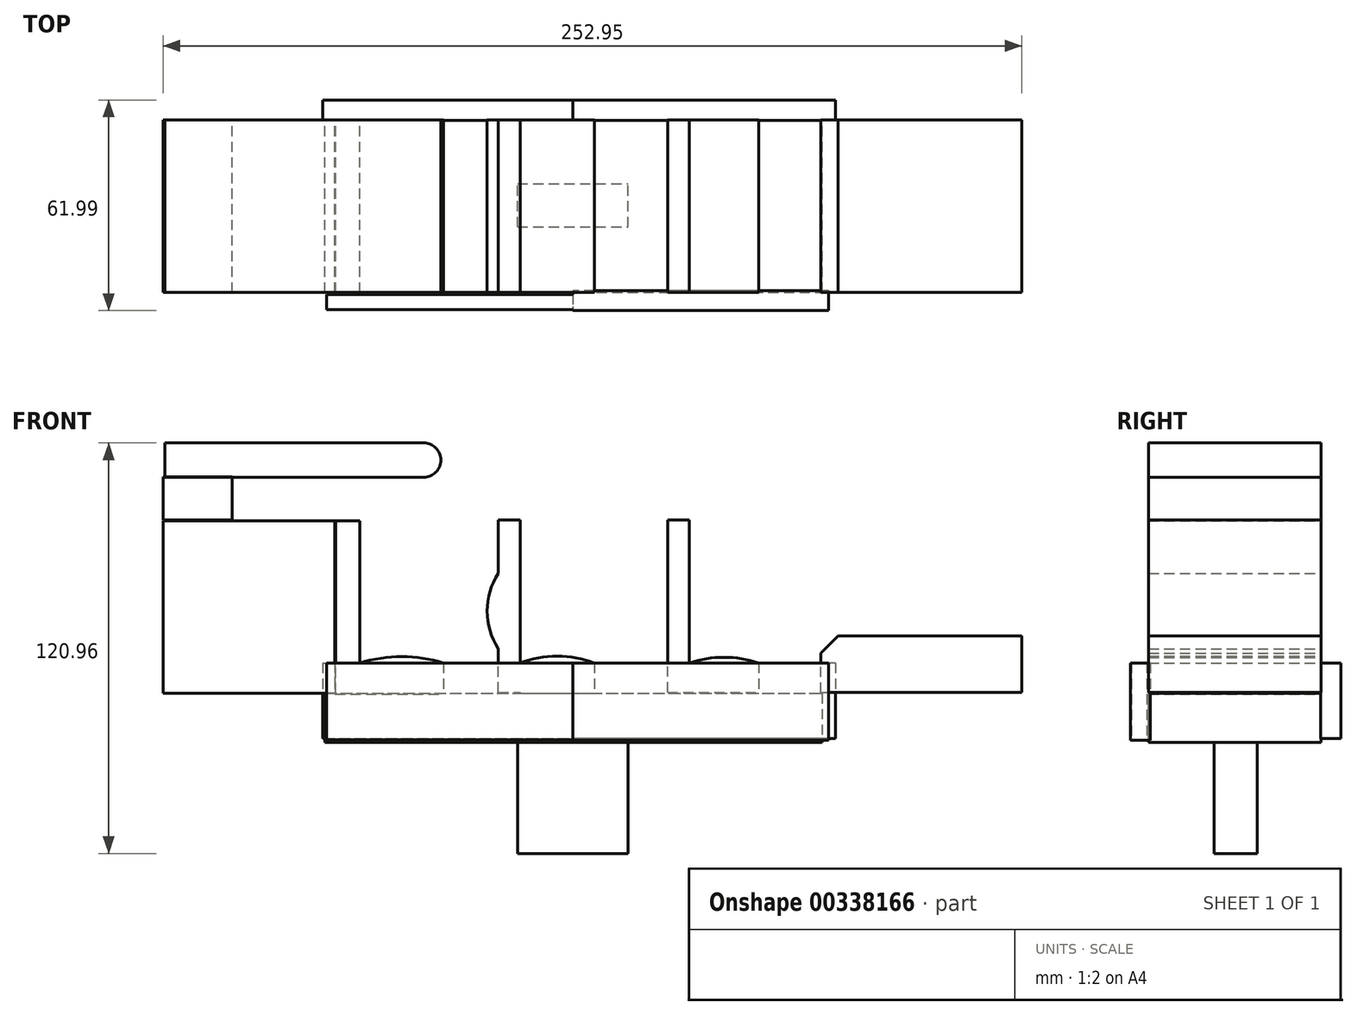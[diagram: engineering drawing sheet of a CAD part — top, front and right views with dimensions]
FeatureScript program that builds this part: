
annotation { "Feature Type Name" : "Feature", "Feature Type Description" : "" }
export const myFeature = defineFeature(function(context is Context, id is Id, definition is map)
    precondition{}
    {
        {
            var Q0;
            Q0=qCreatedBy(makeId("Front.planeOp"),FACE);
            var sketch = newSketch(context, id + "F0", { "sketchPlane" : qUnion([Q0])});
            skLineSegment(sketch, "E0.bottom", {"start": v(-72.96, -23.33) * mm, "end": v(-22.26, -23.33) * mm});
            skLineSegment(sketch, "E0.top", {"start": v(-72.96, -8.96) * mm, "end": v(-22.26, -8.96) * mm});
            skLineSegment(sketch, "E0.left", {"start": v(-72.96, -23.33) * mm, "end": v(-72.96, -8.96) * mm});
            skLineSegment(sketch, "E0.right", {"start": v(-22.26, -23.33) * mm, "end": v(-22.26, -8.96) * mm});
            skLineSegment(sketch, "E1.bottom", {"start": v(-22.26, -8.96) * mm, "end": v(28.07, -8.96) * mm});
            skLineSegment(sketch, "E1.top", {"start": v(-22.26, -23.33) * mm, "end": v(28.07, -23.33) * mm});
            skLineSegment(sketch, "E1.left", {"start": v(-22.26, -8.96) * mm, "end": v(-22.26, -23.33) * mm});
            skLineSegment(sketch, "E1.right", {"start": v(28.07, -8.96) * mm, "end": v(28.07, -23.33) * mm});
            skLineSegment(sketch, "E2.bottom", {"start": v(28.07, -8.96) * mm, "end": v(73.47, -8.96) * mm});
            skLineSegment(sketch, "E2.top", {"start": v(28.07, -23.33) * mm, "end": v(73.47, -23.33) * mm});
            skLineSegment(sketch, "E2.right", {"start": v(73.47, -8.96) * mm, "end": v(73.47, -23.33) * mm});
            skSolve(sketch);
        }
        {
            var Q0;
            Q0=qCreatedBy(makeId("Front.planeOp"),FACE);
            var sketch = newSketch(context, id + "F1", { "sketchPlane" : qUnion([Q0])});
            skLineSegment(sketch, "E3.bottom", {"start": v(-69.87, -8.9) * mm, "end": v(-120.67, -8.9) * mm});
            skLineSegment(sketch, "E3.top", {"start": v(-69.87, 41.9) * mm, "end": v(-120.67, 41.9) * mm});
            skLineSegment(sketch, "E3.left", {"start": v(-69.87, -8.9) * mm, "end": v(-69.87, 41.9) * mm});
            skLineSegment(sketch, "E3.right", {"start": v(-120.67, -8.9) * mm, "end": v(-120.67, 41.9) * mm});
            skSolve(sketch);
        }
        {
            var Q0;
            Q0=qCreatedBy(makeId("Front.planeOp"),FACE);
            var sketch = newSketch(context, id + "F2", { "sketchPlane" : qUnion([Q0])});
            skLineSegment(sketch, "E4.bottom", {"start": v(-70.05, 41.85) * mm, "end": v(-62.64, 41.85) * mm});
            skLineSegment(sketch, "E4.top", {"start": v(-70.05, -9.16) * mm, "end": v(-62.64, -9.16) * mm});
            skLineSegment(sketch, "E4.left", {"start": v(-70.05, 41.85) * mm, "end": v(-70.05, -9.16) * mm});
            skLineSegment(sketch, "E4.right", {"start": v(-62.64, 41.85) * mm, "end": v(-62.64, -9.16) * mm});
            skLineSegment(sketch, "E5.bottom", {"start": v(-62.64, 0) * mm, "end": v(-38.02, 0) * mm});
            skLineSegment(sketch, "E5.top", {"start": v(-62.64, -9.16) * mm, "end": v(-38.02, -9.16) * mm});
            skLineSegment(sketch, "E5.left", {"start": v(-62.64, 0) * mm, "end": v(-62.64, -9.16) * mm});
            skLineSegment(sketch, "E5.right", {"start": v(-38.02, 0) * mm, "end": v(-38.02, -9.16) * mm});
            skArc(sketch, "E6", {"start": v(-38.02, 0) * mm, "mid": v(-50.33, 1.9) * mm, "end": v(-62.64, 0) * mm});
            skSolve(sketch);
        }
        {
            var Q0;
            Q0=qCreatedBy(makeId("Front.planeOp"),FACE);
            var sketch = newSketch(context, id + "F3", { "sketchPlane" : qUnion([Q0])});
            skLineSegment(sketch, "E7.bottom", {"start": v(-120.63, 42.12) * mm, "end": v(-100.31, 42.12) * mm});
            skLineSegment(sketch, "E7.top", {"start": v(-120.63, 54.82) * mm, "end": v(-100.31, 54.82) * mm});
            skLineSegment(sketch, "E7.left", {"start": v(-120.63, 42.12) * mm, "end": v(-120.63, 54.82) * mm});
            skLineSegment(sketch, "E7.right", {"start": v(-100.31, 42.12) * mm, "end": v(-100.31, 54.82) * mm});
            skSolve(sketch);
        }
        {
            var Q0;
            Q0=qCreatedBy(makeId("Front.planeOp"),FACE);
            var sketch = newSketch(context, id + "F4", { "sketchPlane" : qUnion([Q0])});
            skLineSegment(sketch, "E8", {"start": v(-120.13, 54.7) * mm, "end": v(-43.93, 54.7) * mm});
            skLineSegment(sketch, "E9", {"start": v(-120.13, 54.7) * mm, "end": v(-120.13, 64.85) * mm});
            skLineSegment(sketch, "E10", {"start": v(-120.13, 64.85) * mm, "end": v(-43.93, 64.85) * mm});
            skArc(sketch, "E11", {"start": v(-43.93, 54.7) * mm, "mid": v(-38.85, 59.77) * mm, "end": v(-43.93, 64.85) * mm});
            skSolve(sketch);
        }
        {
            var Q0;
            Q0=qCreatedBy(makeId("Front.planeOp"),FACE);
            var sketch = newSketch(context, id + "F5", { "sketchPlane" : qUnion([Q0])});
            skLineSegment(sketch, "E12.bottom", {"start": v(-21.9, -8.64) * mm, "end": v(-15.49, -8.64) * mm});
            skLineSegment(sketch, "E12.top", {"start": v(-21.9, 42.16) * mm, "end": v(-15.49, 42.16) * mm});
            skLineSegment(sketch, "E12.left", {"start": v(-21.9, -8.64) * mm, "end": v(-21.9, 42.16) * mm});
            skLineSegment(sketch, "E12.right", {"start": v(-15.49, -8.64) * mm, "end": v(-15.49, 42.16) * mm});
            skLineSegment(sketch, "E13.bottom", {"start": v(-15.49, 0) * mm, "end": v(6.37, 0) * mm});
            skLineSegment(sketch, "E13.top", {"start": v(-15.49, -8.9) * mm, "end": v(6.37, -8.9) * mm});
            skLineSegment(sketch, "E13.left", {"start": v(-15.49, 0) * mm, "end": v(-15.49, -8.9) * mm});
            skLineSegment(sketch, "E13.right", {"start": v(6.37, 0) * mm, "end": v(6.37, -8.9) * mm});
            skArc(sketch, "E14", {"start": v(6.37, 0) * mm, "mid": v(-4.56, 2.03) * mm, "end": v(-15.49, 0) * mm});
            skArc(sketch, "E15", {"start": v(-21.9, 26.38) * mm, "mid": v(-25.18, 15.3) * mm, "end": v(-21.9, 4.23) * mm});
            skSolve(sketch);
        }
        {
            var Q0;
            Q0=qCreatedBy(makeId("Front.planeOp"),FACE);
            var sketch = newSketch(context, id + "F6", { "sketchPlane" : qUnion([Q0])});
            skLineSegment(sketch, "E16.bottom", {"start": v(73.12, -8.71) * mm, "end": v(132.28, -8.71) * mm});
            skLineSegment(sketch, "E16.top", {"start": v(73.12, 8.02) * mm, "end": v(132.28, 8.02) * mm});
            skLineSegment(sketch, "E16.left", {"start": v(73.12, -8.71) * mm, "end": v(73.12, 8.02) * mm});
            skLineSegment(sketch, "E16.right", {"start": v(132.28, -8.71) * mm, "end": v(132.28, 8.02) * mm});
            skSolve(sketch);
        }
        {
            var Q0;
            Q0=qCreatedBy(makeId("Front.planeOp"),FACE);
            var sketch = newSketch(context, id + "F7", { "sketchPlane" : qUnion([Q0])});
            skLineSegment(sketch, "E17.bottom", {"start": v(27.94, -8.6) * mm, "end": v(34.35, -8.6) * mm});
            skLineSegment(sketch, "E17.top", {"start": v(27.94, 42.12) * mm, "end": v(34.35, 42.12) * mm});
            skLineSegment(sketch, "E17.left", {"start": v(27.94, -8.6) * mm, "end": v(27.94, 42.12) * mm});
            skLineSegment(sketch, "E17.right", {"start": v(34.35, -8.6) * mm, "end": v(34.35, 42.12) * mm});
            skLineSegment(sketch, "E18.bottom", {"start": v(34.35, 0) * mm, "end": v(54.75, 0) * mm});
            skLineSegment(sketch, "E18.top", {"start": v(34.35, -8.6) * mm, "end": v(54.75, -8.6) * mm});
            skLineSegment(sketch, "E18.left", {"start": v(34.35, 0) * mm, "end": v(34.35, -8.6) * mm});
            skLineSegment(sketch, "E18.right", {"start": v(54.75, 0) * mm, "end": v(54.75, -8.6) * mm});
            skArc(sketch, "E19", {"start": v(54.75, 0) * mm, "mid": v(44.55, 1.67) * mm, "end": v(34.35, 0) * mm});
            skSolve(sketch);
        }
        {
            var Q0;
            Q0=makeQuery(id+"F7.imprint","IMPRINT",FACE,{"disambiguationData":[TD([[makeQuery(id+"F7.imprint","IMPRINT",EDGE,{"derivedFrom":sQuery(id+"F7.wireOp",EDGE,"E17.bottom")}),1.0]])]});
            var Q1;
            {var subQ4=sQuery(id+"F5.wireOp",EDGE,"E12.bottom");Q1=makeQuery(id+"F5.imprint","IMPRINT",FACE,{"disambiguationData":[TD([[makeQuery(id+"F5.imprint","IMPRINT",EDGE,{"derivedFrom":subQ4}),1.0]])]});}
            var Q2;
            {var subQ0=sQuery(id+"F5.wireOp",EDGE,"E15");Q2=makeQuery(id+"F5.imprint","IMPRINT",FACE,{"disambiguationData":[TD([[makeQuery(id+"F5.imprint","IMPRINT",EDGE,{"derivedFrom":subQ0}),1.0]])]});}
            var Q3;
            {var subQ3=sQuery(id+"F5.wireOp",EDGE,"E13.bottom");Q3=makeQuery(id+"F5.imprint","IMPRINT",FACE,{"disambiguationData":[TD([[makeQuery(id+"F5.imprint","IMPRINT",EDGE,{"derivedFrom":subQ3}),-1.0]])]});}
            var Q4;
            Q4=makeQuery(id+"F5.imprint","IMPRINT",FACE,{"disambiguationData":[TD([[makeQuery(id+"F5.imprint","IMPRINT",EDGE,{"derivedFrom":sQuery(id+"F5.wireOp",EDGE,"E13.bottom")}),1.0]])]});
            var Q5;
            Q5=makeQuery(id+"F7.imprint","IMPRINT",FACE,{"disambiguationData":[TD([[makeQuery(id+"F7.imprint","IMPRINT",EDGE,{"derivedFrom":sQuery(id+"F7.wireOp",EDGE,"E18.bottom")}),-1.0]])]});
            var Q6;
            Q6=makeQuery(id+"F7.imprint","IMPRINT",FACE,{"disambiguationData":[TD([[makeQuery(id+"F7.imprint","IMPRINT",EDGE,{"derivedFrom":sQuery(id+"F7.wireOp",EDGE,"E18.bottom")}),1.0]])]});
            var Q7;
            Q7=makeQuery(id+"F6.imprint","IMPRINT",FACE,{"disambiguationData":[TD([[makeQuery(id+"F6.imprint","IMPRINT",EDGE,{"derivedFrom":sQuery(id+"F6.wireOp",EDGE,"E16.bottom")}),1.0]])]});
            var Q8;
            Q8=makeQuery(id+"F0.imprint","IMPRINT",FACE,{"disambiguationData":[TD([[makeQuery(id+"F0.imprint","IMPRINT",EDGE,{"derivedFrom":sQuery(id+"F0.wireOp",EDGE,"E1.bottom")}),-1.0]])]});
            var Q9;
            Q9=makeQuery(id+"F0.imprint","IMPRINT",FACE,{"disambiguationData":[TD([[makeQuery(id+"F0.imprint","IMPRINT",EDGE,{"derivedFrom":sQuery(id+"F0.wireOp",EDGE,"E2.bottom")}),-1.0]])]});
            var Q10;
            Q10=makeQuery(id+"F0.imprint","IMPRINT",FACE,{"disambiguationData":[TD([[makeQuery(id+"F0.imprint","IMPRINT",EDGE,{"derivedFrom":sQuery(id+"F0.wireOp",EDGE,"E0.bottom")}),1.0]])]});
            var Q11;
            Q11=makeQuery(id+"F2.imprint","IMPRINT",FACE,{"disambiguationData":[TD([[makeQuery(id+"F2.imprint","IMPRINT",EDGE,{"derivedFrom":sQuery(id+"F2.wireOp",EDGE,"E5.bottom")}),-1.0]])]});
            var Q12;
            Q12=makeQuery(id+"F2.imprint","IMPRINT",FACE,{"disambiguationData":[TD([[makeQuery(id+"F2.imprint","IMPRINT",EDGE,{"derivedFrom":sQuery(id+"F2.wireOp",EDGE,"E5.bottom")}),1.0]])]});
            var Q13;
            Q13=makeQuery(id+"F2.imprint","IMPRINT",FACE,{"disambiguationData":[TD([[makeQuery(id+"F2.imprint","IMPRINT",EDGE,{"derivedFrom":sQuery(id+"F2.wireOp",EDGE,"E4.bottom")}),-1.0]])]});
            var Q14;
            Q14=makeQuery(id+"F1.imprint","IMPRINT",FACE,{"disambiguationData":[TD([[makeQuery(id+"F1.imprint","IMPRINT",EDGE,{"derivedFrom":sQuery(id+"F1.wireOp",EDGE,"E3.bottom")}),-1.0]])]});
            var Q15;
            Q15=makeQuery(id+"F3.imprint","IMPRINT",FACE,{"disambiguationData":[TD([[makeQuery(id+"F3.imprint","IMPRINT",EDGE,{"derivedFrom":sQuery(id+"F3.wireOp",EDGE,"E7.bottom")}),1.0]])]});
            var Q16;
            Q16=makeQuery(id+"F4.imprint","IMPRINT",FACE,{"disambiguationData":[TD([[makeQuery(id+"F4.imprint","IMPRINT",EDGE,{"derivedFrom":sQuery(id+"F4.wireOp",EDGE,"E8")}),1.0]])]});
            var Q17;
            Q17=makeQuery(id+"F4.imprint","IMPRINT",FACE,{"disambiguationData":[TD([[makeQuery(id+"F4.imprint","IMPRINT",EDGE,{"derivedFrom":sQuery(id+"F4.wireOp",EDGE,"E8")}),1.0]])]});
            extrude(context, id + "F8", {"entities" : qUnion([Q0, Q1, Q2, Q3, Q4, Q5, Q6, Q7, Q8, Q9, Q10, Q11, Q12, Q13, Q14, Q15, Q16, Q17]), "endBound" : BoundingType.SYMMETRIC, "depth" : 50.8 * mm});
        }
        {
            var Q0;
            Q0=qCreatedBy(makeId("Right.planeOp"),FACE);
            var sketch = newSketch(context, id + "F9", { "sketchPlane" : qUnion([Q0])});
            skLineSegment(sketch, "E20.bottom", {"start": v(-6.12, -23.09) * mm, "end": v(6.58, -23.09) * mm});
            skLineSegment(sketch, "E20.top", {"start": v(-6.12, -56.1) * mm, "end": v(6.58, -56.1) * mm});
            skLineSegment(sketch, "E20.left", {"start": v(-6.12, -23.09) * mm, "end": v(-6.12, -56.1) * mm});
            skLineSegment(sketch, "E20.right", {"start": v(6.58, -23.09) * mm, "end": v(6.58, -56.1) * mm});
            skSolve(sketch);
        }
        {
            var Q0;
            Q0=makeQuery(id+"F9.imprint","IMPRINT",FACE,{"disambiguationData":[TD([[makeQuery(id+"F9.imprint","IMPRINT",EDGE,{"derivedFrom":sQuery(id+"F9.wireOp",EDGE,"E20.bottom")}),-1.0]])]});
            extrude(context, id + "F10", {"entities" : qUnion([Q0]), "operationType" : NewBodyOperationType.ADD, "endBound" : BoundingType.SYMMETRIC, "oppositeDirection" : true, "depth" : 32.5 * mm});
        }
        {
            var Q0;
            Q0=makeQuery(id+"F8.opExtrude","SWEPT_EDGE",EDGE,{"disambiguationData":[OSD([sQuery(id+"F6.wireOp",EDGE,"E16.top"),sQuery(id+"F6.wireOp",EDGE,"E16.left")])]});
            chamfer(context, id + "F11", {"entities" : qUnion([Q0]), "width" : 5.08 * mm, "tangentPropagation" : true});
        }
        {
            var Q0;
            Q0=qCreatedBy(makeId("Right.planeOp"),FACE);
            var sketch = newSketch(context, id + "F12", { "sketchPlane" : qUnion([Q0])});
            skLineSegment(sketch, "E21.bottom", {"start": v(25.28, 0) * mm, "end": v(31.26, 0) * mm});
            skLineSegment(sketch, "E21.top", {"start": v(25.28, -22.27) * mm, "end": v(31.26, -22.27) * mm});
            skLineSegment(sketch, "E21.left", {"start": v(25.28, 0) * mm, "end": v(25.28, -22.27) * mm});
            skLineSegment(sketch, "E21.right", {"start": v(31.26, 0) * mm, "end": v(31.26, -22.27) * mm});
            skSolve(sketch);
        }
        {
            var Q0;
            Q0=qCreatedBy(makeId("Right.planeOp"),FACE);
            var sketch = newSketch(context, id + "F13", { "sketchPlane" : qUnion([Q0])});
            skLineSegment(sketch, "E22.bottom", {"start": v(-24.91, 0) * mm, "end": v(-30.73, 0) * mm});
            skLineSegment(sketch, "E22.top", {"start": v(-24.91, -22.75) * mm, "end": v(-30.73, -22.75) * mm});
            skLineSegment(sketch, "E22.left", {"start": v(-24.91, 0) * mm, "end": v(-24.91, -22.75) * mm});
            skLineSegment(sketch, "E22.right", {"start": v(-30.73, 0) * mm, "end": v(-30.73, -22.75) * mm});
            skSolve(sketch);
        }
        {
            var Q0;
            Q0=makeQuery(id+"F12.imprint","IMPRINT",FACE,{"disambiguationData":[TD([[makeQuery(id+"F12.imprint","IMPRINT",EDGE,{"derivedFrom":sQuery(id+"F12.wireOp",EDGE,"E21.bottom")}),-1.0]])]});
            extrude(context, id + "F14", {"entities" : qUnion([Q0]), "depth" : 77.43 * mm});
        }
        {
            var Q0;
            Q0=makeQuery(id+"F13.imprint","IMPRINT",FACE,{"disambiguationData":[TD([[makeQuery(id+"F13.imprint","IMPRINT",EDGE,{"derivedFrom":sQuery(id+"F13.wireOp",EDGE,"E22.bottom")}),1.0]])]});
            extrude(context, id + "F15", {"entities" : qUnion([Q0]), "depth" : 75.3 * mm});
        }
        {
            var Q0;
            Q0=qCreatedBy(makeId("Right.planeOp"),FACE);
            var sketch = newSketch(context, id + "F16", { "sketchPlane" : qUnion([Q0])});
            skLineSegment(sketch, "E23.bottom", {"start": v(-26, 0) * mm, "end": v(-30.5, 0) * mm});
            skLineSegment(sketch, "E23.top", {"start": v(-26, -22.65) * mm, "end": v(-30.5, -22.65) * mm});
            skLineSegment(sketch, "E23.left", {"start": v(-26, 0) * mm, "end": v(-26, -22.65) * mm});
            skLineSegment(sketch, "E23.right", {"start": v(-30.5, 0) * mm, "end": v(-30.5, -22.65) * mm});
            skLineSegment(sketch, "E24.bottom", {"start": v(30.93, 0) * mm, "end": v(24.97, 0) * mm});
            skLineSegment(sketch, "E24.top", {"start": v(30.93, -22.2) * mm, "end": v(24.97, -22.2) * mm});
            skLineSegment(sketch, "E24.left", {"start": v(30.93, 0) * mm, "end": v(30.93, -22.2) * mm});
            skLineSegment(sketch, "E24.right", {"start": v(24.97, 0) * mm, "end": v(24.97, -22.2) * mm});
            skSolve(sketch);
        }
        {
            var Q0;
            Q0=makeQuery(id+"F16.imprint","IMPRINT",FACE,{"disambiguationData":[TD([[makeQuery(id+"F16.imprint","IMPRINT",EDGE,{"derivedFrom":sQuery(id+"F16.wireOp",EDGE,"E23.bottom")}),1.0]])]});
            extrude(context, id + "F17", {"entities" : qUnion([Q0]), "operationType" : NewBodyOperationType.ADD, "oppositeDirection" : true, "depth" : 72.46 * mm});
        }
        {
            var Q0;
            Q0=makeQuery(id+"F14.opExtrude","CAP_FACE",FACE,{"disambiguationData":[OSD([sQuery(id+"F12.wireOp",EDGE,"E21.bottom"),sQuery(id+"F12.wireOp",EDGE,"E21.top"),sQuery(id+"F12.wireOp",EDGE,"E21.left"),sQuery(id+"F12.wireOp",EDGE,"E21.right")])],"isStart":true});
            extrude(context, id + "F18", {"entities" : qUnion([Q0]), "depth" : 73.57 * mm});
        }
    });
